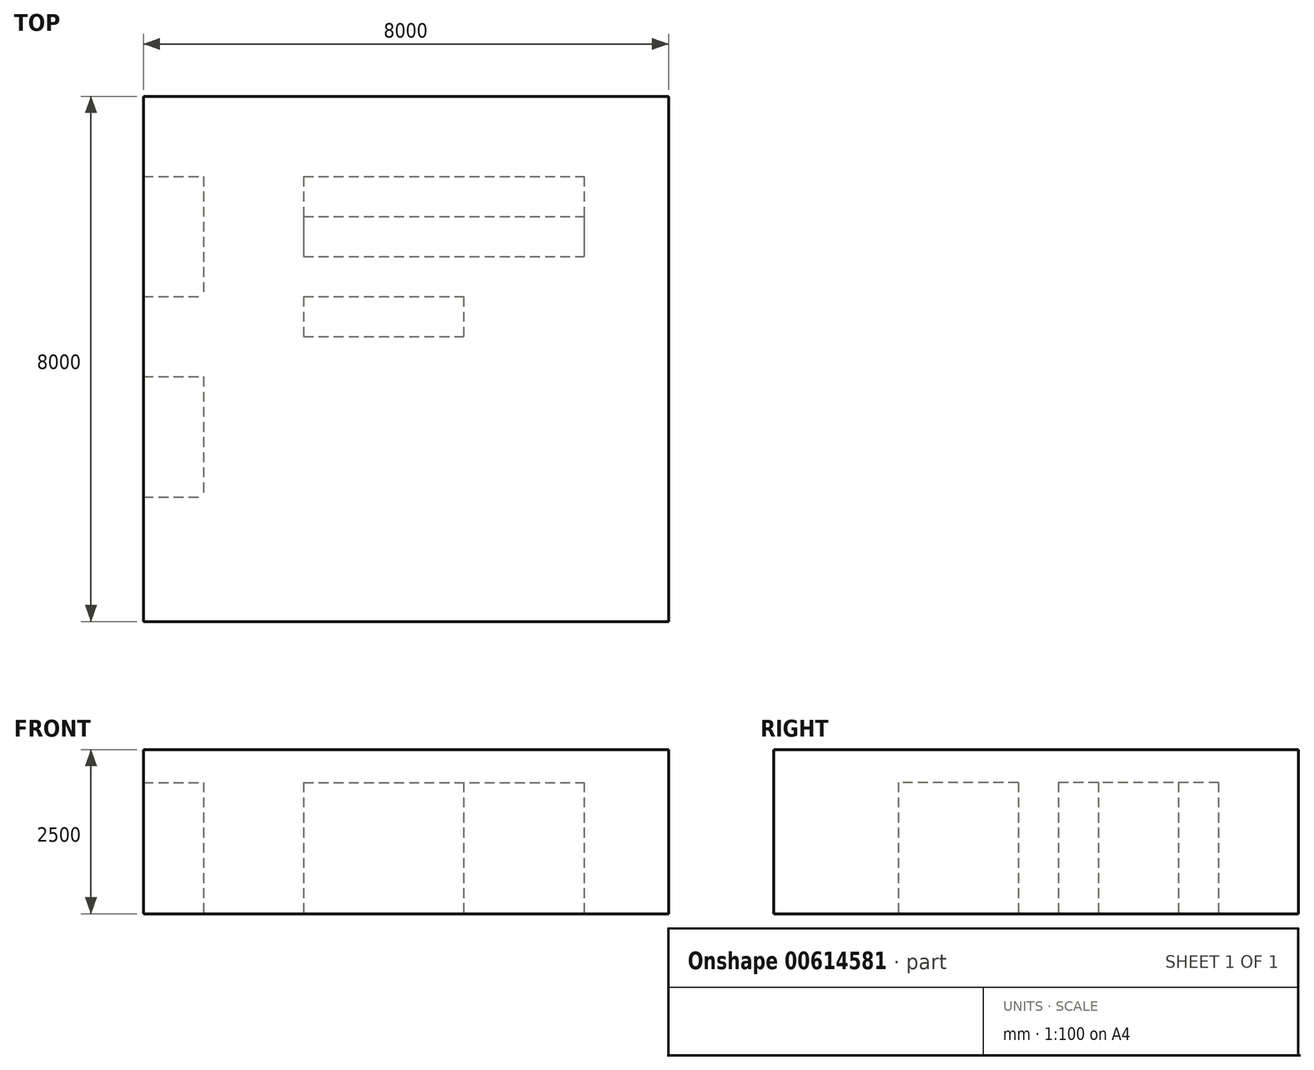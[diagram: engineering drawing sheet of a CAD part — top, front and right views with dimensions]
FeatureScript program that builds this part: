
annotation { "Feature Type Name" : "Feature", "Feature Type Description" : "" }
export const myFeature = defineFeature(function(context is Context, id is Id, definition is map)
    precondition{}
    {
        {
            var Q0;
            Q0=qCreatedBy(makeId("Top.planeOp"),FACE);
            var sketch = newSketch(context, id + "F0", { "sketchPlane" : qUnion([Q0])});
            skLineSegment(sketch, "E0.bottom", {"start": v(0, 0) * mm, "end": v(8000, 0) * mm});
            skLineSegment(sketch, "E0.top", {"start": v(0, -8000) * mm, "end": v(8000, -8000) * mm});
            skLineSegment(sketch, "E0.left", {"start": v(0, 0) * mm, "end": v(0, -8000) * mm});
            skLineSegment(sketch, "E0.right", {"start": v(8000, 0) * mm, "end": v(8000, -8000) * mm});
            skLineSegment(sketch, "E1.bottom", {"start": v(0, 0) * mm, "end": v(610, 0) * mm, "construction": true});
            skLineSegment(sketch, "E1.top", {"start": v(0, -610) * mm, "end": v(610, -610) * mm, "construction": true});
            skLineSegment(sketch, "E1.left", {"start": v(0, 0) * mm, "end": v(0, -610) * mm, "construction": true});
            skLineSegment(sketch, "E1.right", {"start": v(610, 0) * mm, "end": v(610, -610) * mm, "construction": true});
            skLineSegment(sketch, "E2.0.1.0", {"start": v(0, -1220) * mm, "end": v(610, -1220) * mm, "construction": true});
            skLineSegment(sketch, "E2.0.1.1", {"start": v(610, -610) * mm, "end": v(610, -1220) * mm, "construction": true});
            skLineSegment(sketch, "E2.0.2.0", {"start": v(0, -1830) * mm, "end": v(610, -1830) * mm, "construction": true});
            skLineSegment(sketch, "E2.0.2.1", {"start": v(610, -1220) * mm, "end": v(610, -1830) * mm, "construction": true});
            skLineSegment(sketch, "E2.0.3.0", {"start": v(0, -2440) * mm, "end": v(610, -2440) * mm, "construction": true});
            skLineSegment(sketch, "E2.0.3.1", {"start": v(610, -1830) * mm, "end": v(610, -2440) * mm, "construction": true});
            skLineSegment(sketch, "E2.0.4.0", {"start": v(0, -3050) * mm, "end": v(610, -3050) * mm, "construction": true});
            skLineSegment(sketch, "E2.0.4.1", {"start": v(610, -2440) * mm, "end": v(610, -3050) * mm, "construction": true});
            skLineSegment(sketch, "E2.0.5.0", {"start": v(0, -3660) * mm, "end": v(610, -3660) * mm, "construction": true});
            skLineSegment(sketch, "E2.0.5.1", {"start": v(610, -3050) * mm, "end": v(610, -3660) * mm, "construction": true});
            skLineSegment(sketch, "E2.0.6.0", {"start": v(0, -4270) * mm, "end": v(610, -4270) * mm, "construction": true});
            skLineSegment(sketch, "E2.0.6.1", {"start": v(610, -3660) * mm, "end": v(610, -4270) * mm, "construction": true});
            skLineSegment(sketch, "E2.0.7.0", {"start": v(0, -4880) * mm, "end": v(610, -4880) * mm, "construction": true});
            skLineSegment(sketch, "E2.0.7.1", {"start": v(610, -4270) * mm, "end": v(610, -4880) * mm, "construction": true});
            skLineSegment(sketch, "E2.0.8.0", {"start": v(0, -5490) * mm, "end": v(610, -5490) * mm, "construction": true});
            skLineSegment(sketch, "E2.0.8.1", {"start": v(610, -4880) * mm, "end": v(610, -5490) * mm, "construction": true});
            skLineSegment(sketch, "E2.0.9.0", {"start": v(0, -6100) * mm, "end": v(610, -6100) * mm, "construction": true});
            skLineSegment(sketch, "E2.0.9.1", {"start": v(610, -5490) * mm, "end": v(610, -6100) * mm, "construction": true});
            skLineSegment(sketch, "E2.0.10.0", {"start": v(0, -6710) * mm, "end": v(610, -6710) * mm, "construction": true});
            skLineSegment(sketch, "E2.0.10.1", {"start": v(610, -6100) * mm, "end": v(610, -6710) * mm, "construction": true});
            skLineSegment(sketch, "E2.0.11.0", {"start": v(0, -7320) * mm, "end": v(610, -7320) * mm, "construction": true});
            skLineSegment(sketch, "E2.0.11.1", {"start": v(610, -6710) * mm, "end": v(610, -7320) * mm, "construction": true});
            skLineSegment(sketch, "E2.0.12.0", {"start": v(0, -7930) * mm, "end": v(610, -7930) * mm, "construction": true});
            skLineSegment(sketch, "E2.0.12.1", {"start": v(610, -7320) * mm, "end": v(610, -7930) * mm, "construction": true});
            skLineSegment(sketch, "E2.1.0.0", {"start": v(610, -610) * mm, "end": v(1220, -610) * mm, "construction": true});
            skLineSegment(sketch, "E2.1.0.1", {"start": v(1220, 0) * mm, "end": v(1220, -610) * mm, "construction": true});
            skLineSegment(sketch, "E2.1.1.0", {"start": v(610, -1220) * mm, "end": v(1220, -1220) * mm, "construction": true});
            skLineSegment(sketch, "E2.1.1.1", {"start": v(1220, -610) * mm, "end": v(1220, -1220) * mm, "construction": true});
            skLineSegment(sketch, "E2.1.2.0", {"start": v(610, -1830) * mm, "end": v(1220, -1830) * mm, "construction": true});
            skLineSegment(sketch, "E2.1.2.1", {"start": v(1220, -1220) * mm, "end": v(1220, -1830) * mm, "construction": true});
            skLineSegment(sketch, "E2.1.3.0", {"start": v(610, -2440) * mm, "end": v(1220, -2440) * mm, "construction": true});
            skLineSegment(sketch, "E2.1.3.1", {"start": v(1220, -1830) * mm, "end": v(1220, -2440) * mm, "construction": true});
            skLineSegment(sketch, "E2.1.4.0", {"start": v(610, -3050) * mm, "end": v(1220, -3050) * mm, "construction": true});
            skLineSegment(sketch, "E2.1.4.1", {"start": v(1220, -2440) * mm, "end": v(1220, -3050) * mm, "construction": true});
            skLineSegment(sketch, "E2.1.5.0", {"start": v(610, -3660) * mm, "end": v(1220, -3660) * mm, "construction": true});
            skLineSegment(sketch, "E2.1.5.1", {"start": v(1220, -3050) * mm, "end": v(1220, -3660) * mm, "construction": true});
            skLineSegment(sketch, "E2.1.6.0", {"start": v(610, -4270) * mm, "end": v(1220, -4270) * mm, "construction": true});
            skLineSegment(sketch, "E2.1.6.1", {"start": v(1220, -3660) * mm, "end": v(1220, -4270) * mm, "construction": true});
            skLineSegment(sketch, "E2.1.7.0", {"start": v(610, -4880) * mm, "end": v(1220, -4880) * mm, "construction": true});
            skLineSegment(sketch, "E2.1.7.1", {"start": v(1220, -4270) * mm, "end": v(1220, -4880) * mm, "construction": true});
            skLineSegment(sketch, "E2.1.8.0", {"start": v(610, -5490) * mm, "end": v(1220, -5490) * mm, "construction": true});
            skLineSegment(sketch, "E2.1.8.1", {"start": v(1220, -4880) * mm, "end": v(1220, -5490) * mm, "construction": true});
            skLineSegment(sketch, "E2.1.9.0", {"start": v(610, -6100) * mm, "end": v(1220, -6100) * mm, "construction": true});
            skLineSegment(sketch, "E2.1.9.1", {"start": v(1220, -5490) * mm, "end": v(1220, -6100) * mm, "construction": true});
            skLineSegment(sketch, "E2.1.10.0", {"start": v(610, -6710) * mm, "end": v(1220, -6710) * mm, "construction": true});
            skLineSegment(sketch, "E2.1.10.1", {"start": v(1220, -6100) * mm, "end": v(1220, -6710) * mm, "construction": true});
            skLineSegment(sketch, "E2.1.11.0", {"start": v(610, -7320) * mm, "end": v(1220, -7320) * mm, "construction": true});
            skLineSegment(sketch, "E2.1.11.1", {"start": v(1220, -6710) * mm, "end": v(1220, -7320) * mm, "construction": true});
            skLineSegment(sketch, "E2.1.12.0", {"start": v(610, -7930) * mm, "end": v(1220, -7930) * mm, "construction": true});
            skLineSegment(sketch, "E2.1.12.1", {"start": v(1220, -7320) * mm, "end": v(1220, -7930) * mm, "construction": true});
            skLineSegment(sketch, "E2.2.0.0", {"start": v(1220, -610) * mm, "end": v(1830, -610) * mm, "construction": true});
            skLineSegment(sketch, "E2.2.0.1", {"start": v(1830, 0) * mm, "end": v(1830, -610) * mm, "construction": true});
            skLineSegment(sketch, "E2.2.1.0", {"start": v(1220, -1220) * mm, "end": v(1830, -1220) * mm, "construction": true});
            skLineSegment(sketch, "E2.2.1.1", {"start": v(1830, -610) * mm, "end": v(1830, -1220) * mm, "construction": true});
            skLineSegment(sketch, "E2.2.2.0", {"start": v(1220, -1830) * mm, "end": v(1830, -1830) * mm, "construction": true});
            skLineSegment(sketch, "E2.2.2.1", {"start": v(1830, -1220) * mm, "end": v(1830, -1830) * mm, "construction": true});
            skLineSegment(sketch, "E2.2.3.0", {"start": v(1220, -2440) * mm, "end": v(1830, -2440) * mm, "construction": true});
            skLineSegment(sketch, "E2.2.3.1", {"start": v(1830, -1830) * mm, "end": v(1830, -2440) * mm, "construction": true});
            skLineSegment(sketch, "E2.2.4.0", {"start": v(1220, -3050) * mm, "end": v(1830, -3050) * mm, "construction": true});
            skLineSegment(sketch, "E2.2.4.1", {"start": v(1830, -2440) * mm, "end": v(1830, -3050) * mm, "construction": true});
            skLineSegment(sketch, "E2.2.5.0", {"start": v(1220, -3660) * mm, "end": v(1830, -3660) * mm, "construction": true});
            skLineSegment(sketch, "E2.2.5.1", {"start": v(1830, -3050) * mm, "end": v(1830, -3660) * mm, "construction": true});
            skLineSegment(sketch, "E2.2.6.0", {"start": v(1220, -4270) * mm, "end": v(1830, -4270) * mm, "construction": true});
            skLineSegment(sketch, "E2.2.6.1", {"start": v(1830, -3660) * mm, "end": v(1830, -4270) * mm, "construction": true});
            skLineSegment(sketch, "E2.2.7.0", {"start": v(1220, -4880) * mm, "end": v(1830, -4880) * mm, "construction": true});
            skLineSegment(sketch, "E2.2.7.1", {"start": v(1830, -4270) * mm, "end": v(1830, -4880) * mm, "construction": true});
            skLineSegment(sketch, "E2.2.8.0", {"start": v(1220, -5490) * mm, "end": v(1830, -5490) * mm, "construction": true});
            skLineSegment(sketch, "E2.2.8.1", {"start": v(1830, -4880) * mm, "end": v(1830, -5490) * mm, "construction": true});
            skLineSegment(sketch, "E2.2.9.0", {"start": v(1220, -6100) * mm, "end": v(1830, -6100) * mm, "construction": true});
            skLineSegment(sketch, "E2.2.9.1", {"start": v(1830, -5490) * mm, "end": v(1830, -6100) * mm, "construction": true});
            skLineSegment(sketch, "E2.2.10.0", {"start": v(1220, -6710) * mm, "end": v(1830, -6710) * mm, "construction": true});
            skLineSegment(sketch, "E2.2.10.1", {"start": v(1830, -6100) * mm, "end": v(1830, -6710) * mm, "construction": true});
            skLineSegment(sketch, "E2.2.11.0", {"start": v(1220, -7320) * mm, "end": v(1830, -7320) * mm, "construction": true});
            skLineSegment(sketch, "E2.2.11.1", {"start": v(1830, -6710) * mm, "end": v(1830, -7320) * mm, "construction": true});
            skLineSegment(sketch, "E2.2.12.0", {"start": v(1220, -7930) * mm, "end": v(1830, -7930) * mm, "construction": true});
            skLineSegment(sketch, "E2.2.12.1", {"start": v(1830, -7320) * mm, "end": v(1830, -7930) * mm, "construction": true});
            skLineSegment(sketch, "E2.3.0.0", {"start": v(1830, -610) * mm, "end": v(2440, -610) * mm, "construction": true});
            skLineSegment(sketch, "E2.3.0.1", {"start": v(2440, 0) * mm, "end": v(2440, -610) * mm, "construction": true});
            skLineSegment(sketch, "E2.3.1.0", {"start": v(1830, -1220) * mm, "end": v(2440, -1220) * mm, "construction": true});
            skLineSegment(sketch, "E2.3.1.1", {"start": v(2440, -610) * mm, "end": v(2440, -1220) * mm, "construction": true});
            skLineSegment(sketch, "E2.3.2.0", {"start": v(1830, -1830) * mm, "end": v(2440, -1830) * mm, "construction": true});
            skLineSegment(sketch, "E2.3.2.1", {"start": v(2440, -1220) * mm, "end": v(2440, -1830) * mm, "construction": true});
            skLineSegment(sketch, "E2.3.3.0", {"start": v(1830, -2440) * mm, "end": v(2440, -2440) * mm, "construction": true});
            skLineSegment(sketch, "E2.3.3.1", {"start": v(2440, -1830) * mm, "end": v(2440, -2440) * mm, "construction": true});
            skLineSegment(sketch, "E2.3.4.0", {"start": v(1830, -3050) * mm, "end": v(2440, -3050) * mm, "construction": true});
            skLineSegment(sketch, "E2.3.4.1", {"start": v(2440, -2440) * mm, "end": v(2440, -3050) * mm, "construction": true});
            skLineSegment(sketch, "E2.3.5.0", {"start": v(1830, -3660) * mm, "end": v(2440, -3660) * mm, "construction": true});
            skLineSegment(sketch, "E2.3.5.1", {"start": v(2440, -3050) * mm, "end": v(2440, -3660) * mm, "construction": true});
            skLineSegment(sketch, "E2.3.6.0", {"start": v(1830, -4270) * mm, "end": v(2440, -4270) * mm, "construction": true});
            skLineSegment(sketch, "E2.3.6.1", {"start": v(2440, -3660) * mm, "end": v(2440, -4270) * mm, "construction": true});
            skLineSegment(sketch, "E2.3.7.0", {"start": v(1830, -4880) * mm, "end": v(2440, -4880) * mm, "construction": true});
            skLineSegment(sketch, "E2.3.7.1", {"start": v(2440, -4270) * mm, "end": v(2440, -4880) * mm, "construction": true});
            skLineSegment(sketch, "E2.3.8.0", {"start": v(1830, -5490) * mm, "end": v(2440, -5490) * mm, "construction": true});
            skLineSegment(sketch, "E2.3.8.1", {"start": v(2440, -4880) * mm, "end": v(2440, -5490) * mm, "construction": true});
            skLineSegment(sketch, "E2.3.9.0", {"start": v(1830, -6100) * mm, "end": v(2440, -6100) * mm, "construction": true});
            skLineSegment(sketch, "E2.3.9.1", {"start": v(2440, -5490) * mm, "end": v(2440, -6100) * mm, "construction": true});
            skLineSegment(sketch, "E2.3.10.0", {"start": v(1830, -6710) * mm, "end": v(2440, -6710) * mm, "construction": true});
            skLineSegment(sketch, "E2.3.10.1", {"start": v(2440, -6100) * mm, "end": v(2440, -6710) * mm, "construction": true});
            skLineSegment(sketch, "E2.3.11.0", {"start": v(1830, -7320) * mm, "end": v(2440, -7320) * mm, "construction": true});
            skLineSegment(sketch, "E2.3.11.1", {"start": v(2440, -6710) * mm, "end": v(2440, -7320) * mm, "construction": true});
            skLineSegment(sketch, "E2.3.12.0", {"start": v(1830, -7930) * mm, "end": v(2440, -7930) * mm, "construction": true});
            skLineSegment(sketch, "E2.3.12.1", {"start": v(2440, -7320) * mm, "end": v(2440, -7930) * mm, "construction": true});
            skLineSegment(sketch, "E2.4.0.0", {"start": v(2440, -610) * mm, "end": v(3050, -610) * mm, "construction": true});
            skLineSegment(sketch, "E2.4.0.1", {"start": v(3050, 0) * mm, "end": v(3050, -610) * mm, "construction": true});
            skLineSegment(sketch, "E2.4.1.0", {"start": v(2440, -1220) * mm, "end": v(3050, -1220) * mm, "construction": true});
            skLineSegment(sketch, "E2.4.1.1", {"start": v(3050, -610) * mm, "end": v(3050, -1220) * mm, "construction": true});
            skLineSegment(sketch, "E2.4.2.0", {"start": v(2440, -1830) * mm, "end": v(3050, -1830) * mm, "construction": true});
            skLineSegment(sketch, "E2.4.2.1", {"start": v(3050, -1220) * mm, "end": v(3050, -1830) * mm, "construction": true});
            skLineSegment(sketch, "E2.4.3.0", {"start": v(2440, -2440) * mm, "end": v(3050, -2440) * mm, "construction": true});
            skLineSegment(sketch, "E2.4.3.1", {"start": v(3050, -1830) * mm, "end": v(3050, -2440) * mm, "construction": true});
            skLineSegment(sketch, "E2.4.4.0", {"start": v(2440, -3050) * mm, "end": v(3050, -3050) * mm, "construction": true});
            skLineSegment(sketch, "E2.4.4.1", {"start": v(3050, -2440) * mm, "end": v(3050, -3050) * mm, "construction": true});
            skLineSegment(sketch, "E2.4.5.0", {"start": v(2440, -3660) * mm, "end": v(3050, -3660) * mm, "construction": true});
            skLineSegment(sketch, "E2.4.5.1", {"start": v(3050, -3050) * mm, "end": v(3050, -3660) * mm, "construction": true});
            skLineSegment(sketch, "E2.4.6.0", {"start": v(2440, -4270) * mm, "end": v(3050, -4270) * mm, "construction": true});
            skLineSegment(sketch, "E2.4.6.1", {"start": v(3050, -3660) * mm, "end": v(3050, -4270) * mm, "construction": true});
            skLineSegment(sketch, "E2.4.7.0", {"start": v(2440, -4880) * mm, "end": v(3050, -4880) * mm, "construction": true});
            skLineSegment(sketch, "E2.4.7.1", {"start": v(3050, -4270) * mm, "end": v(3050, -4880) * mm, "construction": true});
            skLineSegment(sketch, "E2.4.8.0", {"start": v(2440, -5490) * mm, "end": v(3050, -5490) * mm, "construction": true});
            skLineSegment(sketch, "E2.4.8.1", {"start": v(3050, -4880) * mm, "end": v(3050, -5490) * mm, "construction": true});
            skLineSegment(sketch, "E2.4.9.0", {"start": v(2440, -6100) * mm, "end": v(3050, -6100) * mm, "construction": true});
            skLineSegment(sketch, "E2.4.9.1", {"start": v(3050, -5490) * mm, "end": v(3050, -6100) * mm, "construction": true});
            skLineSegment(sketch, "E2.4.10.0", {"start": v(2440, -6710) * mm, "end": v(3050, -6710) * mm, "construction": true});
            skLineSegment(sketch, "E2.4.10.1", {"start": v(3050, -6100) * mm, "end": v(3050, -6710) * mm, "construction": true});
            skLineSegment(sketch, "E2.4.11.0", {"start": v(2440, -7320) * mm, "end": v(3050, -7320) * mm, "construction": true});
            skLineSegment(sketch, "E2.4.11.1", {"start": v(3050, -6710) * mm, "end": v(3050, -7320) * mm, "construction": true});
            skLineSegment(sketch, "E2.4.12.0", {"start": v(2440, -7930) * mm, "end": v(3050, -7930) * mm, "construction": true});
            skLineSegment(sketch, "E2.4.12.1", {"start": v(3050, -7320) * mm, "end": v(3050, -7930) * mm, "construction": true});
            skLineSegment(sketch, "E2.5.0.0", {"start": v(3050, -610) * mm, "end": v(3660, -610) * mm, "construction": true});
            skLineSegment(sketch, "E2.5.0.1", {"start": v(3660, 0) * mm, "end": v(3660, -610) * mm, "construction": true});
            skLineSegment(sketch, "E2.5.1.0", {"start": v(3050, -1220) * mm, "end": v(3660, -1220) * mm, "construction": true});
            skLineSegment(sketch, "E2.5.1.1", {"start": v(3660, -610) * mm, "end": v(3660, -1220) * mm, "construction": true});
            skLineSegment(sketch, "E2.5.2.0", {"start": v(3050, -1830) * mm, "end": v(3660, -1830) * mm, "construction": true});
            skLineSegment(sketch, "E2.5.2.1", {"start": v(3660, -1220) * mm, "end": v(3660, -1830) * mm, "construction": true});
            skLineSegment(sketch, "E2.5.3.0", {"start": v(3050, -2440) * mm, "end": v(3660, -2440) * mm, "construction": true});
            skLineSegment(sketch, "E2.5.3.1", {"start": v(3660, -1830) * mm, "end": v(3660, -2440) * mm, "construction": true});
            skLineSegment(sketch, "E2.5.4.0", {"start": v(3050, -3050) * mm, "end": v(3660, -3050) * mm, "construction": true});
            skLineSegment(sketch, "E2.5.4.1", {"start": v(3660, -2440) * mm, "end": v(3660, -3050) * mm, "construction": true});
            skLineSegment(sketch, "E2.5.5.0", {"start": v(3050, -3660) * mm, "end": v(3660, -3660) * mm, "construction": true});
            skLineSegment(sketch, "E2.5.5.1", {"start": v(3660, -3050) * mm, "end": v(3660, -3660) * mm, "construction": true});
            skLineSegment(sketch, "E2.5.6.0", {"start": v(3050, -4270) * mm, "end": v(3660, -4270) * mm, "construction": true});
            skLineSegment(sketch, "E2.5.6.1", {"start": v(3660, -3660) * mm, "end": v(3660, -4270) * mm, "construction": true});
            skLineSegment(sketch, "E2.5.7.0", {"start": v(3050, -4880) * mm, "end": v(3660, -4880) * mm, "construction": true});
            skLineSegment(sketch, "E2.5.7.1", {"start": v(3660, -4270) * mm, "end": v(3660, -4880) * mm, "construction": true});
            skLineSegment(sketch, "E2.5.8.0", {"start": v(3050, -5490) * mm, "end": v(3660, -5490) * mm, "construction": true});
            skLineSegment(sketch, "E2.5.8.1", {"start": v(3660, -4880) * mm, "end": v(3660, -5490) * mm, "construction": true});
            skLineSegment(sketch, "E2.5.9.0", {"start": v(3050, -6100) * mm, "end": v(3660, -6100) * mm, "construction": true});
            skLineSegment(sketch, "E2.5.9.1", {"start": v(3660, -5490) * mm, "end": v(3660, -6100) * mm, "construction": true});
            skLineSegment(sketch, "E2.5.10.0", {"start": v(3050, -6710) * mm, "end": v(3660, -6710) * mm, "construction": true});
            skLineSegment(sketch, "E2.5.10.1", {"start": v(3660, -6100) * mm, "end": v(3660, -6710) * mm, "construction": true});
            skLineSegment(sketch, "E2.5.11.0", {"start": v(3050, -7320) * mm, "end": v(3660, -7320) * mm, "construction": true});
            skLineSegment(sketch, "E2.5.11.1", {"start": v(3660, -6710) * mm, "end": v(3660, -7320) * mm, "construction": true});
            skLineSegment(sketch, "E2.5.12.0", {"start": v(3050, -7930) * mm, "end": v(3660, -7930) * mm, "construction": true});
            skLineSegment(sketch, "E2.5.12.1", {"start": v(3660, -7320) * mm, "end": v(3660, -7930) * mm, "construction": true});
            skLineSegment(sketch, "E2.6.0.0", {"start": v(3660, -610) * mm, "end": v(4270, -610) * mm, "construction": true});
            skLineSegment(sketch, "E2.6.0.1", {"start": v(4270, 0) * mm, "end": v(4270, -610) * mm, "construction": true});
            skLineSegment(sketch, "E2.6.1.0", {"start": v(3660, -1220) * mm, "end": v(4270, -1220) * mm, "construction": true});
            skLineSegment(sketch, "E2.6.1.1", {"start": v(4270, -610) * mm, "end": v(4270, -1220) * mm, "construction": true});
            skLineSegment(sketch, "E2.6.2.0", {"start": v(3660, -1830) * mm, "end": v(4270, -1830) * mm, "construction": true});
            skLineSegment(sketch, "E2.6.2.1", {"start": v(4270, -1220) * mm, "end": v(4270, -1830) * mm, "construction": true});
            skLineSegment(sketch, "E2.6.3.0", {"start": v(3660, -2440) * mm, "end": v(4270, -2440) * mm, "construction": true});
            skLineSegment(sketch, "E2.6.3.1", {"start": v(4270, -1830) * mm, "end": v(4270, -2440) * mm, "construction": true});
            skLineSegment(sketch, "E2.6.4.0", {"start": v(3660, -3050) * mm, "end": v(4270, -3050) * mm, "construction": true});
            skLineSegment(sketch, "E2.6.4.1", {"start": v(4270, -2440) * mm, "end": v(4270, -3050) * mm, "construction": true});
            skLineSegment(sketch, "E2.6.5.0", {"start": v(3660, -3660) * mm, "end": v(4270, -3660) * mm, "construction": true});
            skLineSegment(sketch, "E2.6.5.1", {"start": v(4270, -3050) * mm, "end": v(4270, -3660) * mm, "construction": true});
            skLineSegment(sketch, "E2.6.6.0", {"start": v(3660, -4270) * mm, "end": v(4270, -4270) * mm, "construction": true});
            skLineSegment(sketch, "E2.6.6.1", {"start": v(4270, -3660) * mm, "end": v(4270, -4270) * mm, "construction": true});
            skLineSegment(sketch, "E2.6.7.0", {"start": v(3660, -4880) * mm, "end": v(4270, -4880) * mm, "construction": true});
            skLineSegment(sketch, "E2.6.7.1", {"start": v(4270, -4270) * mm, "end": v(4270, -4880) * mm, "construction": true});
            skLineSegment(sketch, "E2.6.8.0", {"start": v(3660, -5490) * mm, "end": v(4270, -5490) * mm, "construction": true});
            skLineSegment(sketch, "E2.6.8.1", {"start": v(4270, -4880) * mm, "end": v(4270, -5490) * mm, "construction": true});
            skLineSegment(sketch, "E2.6.9.0", {"start": v(3660, -6100) * mm, "end": v(4270, -6100) * mm, "construction": true});
            skLineSegment(sketch, "E2.6.9.1", {"start": v(4270, -5490) * mm, "end": v(4270, -6100) * mm, "construction": true});
            skLineSegment(sketch, "E2.6.10.0", {"start": v(3660, -6710) * mm, "end": v(4270, -6710) * mm, "construction": true});
            skLineSegment(sketch, "E2.6.10.1", {"start": v(4270, -6100) * mm, "end": v(4270, -6710) * mm, "construction": true});
            skLineSegment(sketch, "E2.6.11.0", {"start": v(3660, -7320) * mm, "end": v(4270, -7320) * mm, "construction": true});
            skLineSegment(sketch, "E2.6.11.1", {"start": v(4270, -6710) * mm, "end": v(4270, -7320) * mm, "construction": true});
            skLineSegment(sketch, "E2.6.12.0", {"start": v(3660, -7930) * mm, "end": v(4270, -7930) * mm, "construction": true});
            skLineSegment(sketch, "E2.6.12.1", {"start": v(4270, -7320) * mm, "end": v(4270, -7930) * mm, "construction": true});
            skLineSegment(sketch, "E2.7.0.0", {"start": v(4270, -610) * mm, "end": v(4880, -610) * mm, "construction": true});
            skLineSegment(sketch, "E2.7.0.1", {"start": v(4880, 0) * mm, "end": v(4880, -610) * mm, "construction": true});
            skLineSegment(sketch, "E2.7.1.0", {"start": v(4270, -1220) * mm, "end": v(4880, -1220) * mm, "construction": true});
            skLineSegment(sketch, "E2.7.1.1", {"start": v(4880, -610) * mm, "end": v(4880, -1220) * mm, "construction": true});
            skLineSegment(sketch, "E2.7.2.0", {"start": v(4270, -1830) * mm, "end": v(4880, -1830) * mm, "construction": true});
            skLineSegment(sketch, "E2.7.2.1", {"start": v(4880, -1220) * mm, "end": v(4880, -1830) * mm, "construction": true});
            skLineSegment(sketch, "E2.7.3.0", {"start": v(4270, -2440) * mm, "end": v(4880, -2440) * mm, "construction": true});
            skLineSegment(sketch, "E2.7.3.1", {"start": v(4880, -1830) * mm, "end": v(4880, -2440) * mm, "construction": true});
            skLineSegment(sketch, "E2.7.4.0", {"start": v(4270, -3050) * mm, "end": v(4880, -3050) * mm, "construction": true});
            skLineSegment(sketch, "E2.7.4.1", {"start": v(4880, -2440) * mm, "end": v(4880, -3050) * mm, "construction": true});
            skLineSegment(sketch, "E2.7.5.0", {"start": v(4270, -3660) * mm, "end": v(4880, -3660) * mm, "construction": true});
            skLineSegment(sketch, "E2.7.5.1", {"start": v(4880, -3050) * mm, "end": v(4880, -3660) * mm, "construction": true});
            skLineSegment(sketch, "E2.7.6.0", {"start": v(4270, -4270) * mm, "end": v(4880, -4270) * mm, "construction": true});
            skLineSegment(sketch, "E2.7.6.1", {"start": v(4880, -3660) * mm, "end": v(4880, -4270) * mm, "construction": true});
            skLineSegment(sketch, "E2.7.7.0", {"start": v(4270, -4880) * mm, "end": v(4880, -4880) * mm, "construction": true});
            skLineSegment(sketch, "E2.7.7.1", {"start": v(4880, -4270) * mm, "end": v(4880, -4880) * mm, "construction": true});
            skLineSegment(sketch, "E2.7.8.0", {"start": v(4270, -5490) * mm, "end": v(4880, -5490) * mm, "construction": true});
            skLineSegment(sketch, "E2.7.8.1", {"start": v(4880, -4880) * mm, "end": v(4880, -5490) * mm, "construction": true});
            skLineSegment(sketch, "E2.7.9.0", {"start": v(4270, -6100) * mm, "end": v(4880, -6100) * mm, "construction": true});
            skLineSegment(sketch, "E2.7.9.1", {"start": v(4880, -5490) * mm, "end": v(4880, -6100) * mm, "construction": true});
            skLineSegment(sketch, "E2.7.10.0", {"start": v(4270, -6710) * mm, "end": v(4880, -6710) * mm, "construction": true});
            skLineSegment(sketch, "E2.7.10.1", {"start": v(4880, -6100) * mm, "end": v(4880, -6710) * mm, "construction": true});
            skLineSegment(sketch, "E2.7.11.0", {"start": v(4270, -7320) * mm, "end": v(4880, -7320) * mm, "construction": true});
            skLineSegment(sketch, "E2.7.11.1", {"start": v(4880, -6710) * mm, "end": v(4880, -7320) * mm, "construction": true});
            skLineSegment(sketch, "E2.7.12.0", {"start": v(4270, -7930) * mm, "end": v(4880, -7930) * mm, "construction": true});
            skLineSegment(sketch, "E2.7.12.1", {"start": v(4880, -7320) * mm, "end": v(4880, -7930) * mm, "construction": true});
            skLineSegment(sketch, "E2.8.0.0", {"start": v(4880, -610) * mm, "end": v(5490, -610) * mm, "construction": true});
            skLineSegment(sketch, "E2.8.0.1", {"start": v(5490, 0) * mm, "end": v(5490, -610) * mm, "construction": true});
            skLineSegment(sketch, "E2.8.1.0", {"start": v(4880, -1220) * mm, "end": v(5490, -1220) * mm, "construction": true});
            skLineSegment(sketch, "E2.8.1.1", {"start": v(5490, -610) * mm, "end": v(5490, -1220) * mm, "construction": true});
            skLineSegment(sketch, "E2.8.2.0", {"start": v(4880, -1830) * mm, "end": v(5490, -1830) * mm, "construction": true});
            skLineSegment(sketch, "E2.8.2.1", {"start": v(5490, -1220) * mm, "end": v(5490, -1830) * mm, "construction": true});
            skLineSegment(sketch, "E2.8.3.0", {"start": v(4880, -2440) * mm, "end": v(5490, -2440) * mm, "construction": true});
            skLineSegment(sketch, "E2.8.3.1", {"start": v(5490, -1830) * mm, "end": v(5490, -2440) * mm, "construction": true});
            skLineSegment(sketch, "E2.8.4.0", {"start": v(4880, -3050) * mm, "end": v(5490, -3050) * mm, "construction": true});
            skLineSegment(sketch, "E2.8.4.1", {"start": v(5490, -2440) * mm, "end": v(5490, -3050) * mm, "construction": true});
            skLineSegment(sketch, "E2.8.5.0", {"start": v(4880, -3660) * mm, "end": v(5490, -3660) * mm, "construction": true});
            skLineSegment(sketch, "E2.8.5.1", {"start": v(5490, -3050) * mm, "end": v(5490, -3660) * mm, "construction": true});
            skLineSegment(sketch, "E2.8.6.0", {"start": v(4880, -4270) * mm, "end": v(5490, -4270) * mm, "construction": true});
            skLineSegment(sketch, "E2.8.6.1", {"start": v(5490, -3660) * mm, "end": v(5490, -4270) * mm, "construction": true});
            skLineSegment(sketch, "E2.8.7.0", {"start": v(4880, -4880) * mm, "end": v(5490, -4880) * mm, "construction": true});
            skLineSegment(sketch, "E2.8.7.1", {"start": v(5490, -4270) * mm, "end": v(5490, -4880) * mm, "construction": true});
            skLineSegment(sketch, "E2.8.8.0", {"start": v(4880, -5490) * mm, "end": v(5490, -5490) * mm, "construction": true});
            skLineSegment(sketch, "E2.8.8.1", {"start": v(5490, -4880) * mm, "end": v(5490, -5490) * mm, "construction": true});
            skLineSegment(sketch, "E2.8.9.0", {"start": v(4880, -6100) * mm, "end": v(5490, -6100) * mm, "construction": true});
            skLineSegment(sketch, "E2.8.9.1", {"start": v(5490, -5490) * mm, "end": v(5490, -6100) * mm, "construction": true});
            skLineSegment(sketch, "E2.8.10.0", {"start": v(4880, -6710) * mm, "end": v(5490, -6710) * mm, "construction": true});
            skLineSegment(sketch, "E2.8.10.1", {"start": v(5490, -6100) * mm, "end": v(5490, -6710) * mm, "construction": true});
            skLineSegment(sketch, "E2.8.11.0", {"start": v(4880, -7320) * mm, "end": v(5490, -7320) * mm, "construction": true});
            skLineSegment(sketch, "E2.8.11.1", {"start": v(5490, -6710) * mm, "end": v(5490, -7320) * mm, "construction": true});
            skLineSegment(sketch, "E2.8.12.0", {"start": v(4880, -7930) * mm, "end": v(5490, -7930) * mm, "construction": true});
            skLineSegment(sketch, "E2.8.12.1", {"start": v(5490, -7320) * mm, "end": v(5490, -7930) * mm, "construction": true});
            skLineSegment(sketch, "E2.9.0.0", {"start": v(5490, -610) * mm, "end": v(6100, -610) * mm, "construction": true});
            skLineSegment(sketch, "E2.9.0.1", {"start": v(6100, 0) * mm, "end": v(6100, -610) * mm, "construction": true});
            skLineSegment(sketch, "E2.9.1.0", {"start": v(5490, -1220) * mm, "end": v(6100, -1220) * mm, "construction": true});
            skLineSegment(sketch, "E2.9.1.1", {"start": v(6100, -610) * mm, "end": v(6100, -1220) * mm, "construction": true});
            skLineSegment(sketch, "E2.9.2.0", {"start": v(5490, -1830) * mm, "end": v(6100, -1830) * mm, "construction": true});
            skLineSegment(sketch, "E2.9.2.1", {"start": v(6100, -1220) * mm, "end": v(6100, -1830) * mm, "construction": true});
            skLineSegment(sketch, "E2.9.3.0", {"start": v(5490, -2440) * mm, "end": v(6100, -2440) * mm, "construction": true});
            skLineSegment(sketch, "E2.9.3.1", {"start": v(6100, -1830) * mm, "end": v(6100, -2440) * mm, "construction": true});
            skLineSegment(sketch, "E2.9.4.0", {"start": v(5490, -3050) * mm, "end": v(6100, -3050) * mm, "construction": true});
            skLineSegment(sketch, "E2.9.4.1", {"start": v(6100, -2440) * mm, "end": v(6100, -3050) * mm, "construction": true});
            skLineSegment(sketch, "E2.9.5.0", {"start": v(5490, -3660) * mm, "end": v(6100, -3660) * mm, "construction": true});
            skLineSegment(sketch, "E2.9.5.1", {"start": v(6100, -3050) * mm, "end": v(6100, -3660) * mm, "construction": true});
            skLineSegment(sketch, "E2.9.6.0", {"start": v(5490, -4270) * mm, "end": v(6100, -4270) * mm, "construction": true});
            skLineSegment(sketch, "E2.9.6.1", {"start": v(6100, -3660) * mm, "end": v(6100, -4270) * mm, "construction": true});
            skLineSegment(sketch, "E2.9.7.0", {"start": v(5490, -4880) * mm, "end": v(6100, -4880) * mm, "construction": true});
            skLineSegment(sketch, "E2.9.7.1", {"start": v(6100, -4270) * mm, "end": v(6100, -4880) * mm, "construction": true});
            skLineSegment(sketch, "E2.9.8.0", {"start": v(5490, -5490) * mm, "end": v(6100, -5490) * mm, "construction": true});
            skLineSegment(sketch, "E2.9.8.1", {"start": v(6100, -4880) * mm, "end": v(6100, -5490) * mm, "construction": true});
            skLineSegment(sketch, "E2.9.9.0", {"start": v(5490, -6100) * mm, "end": v(6100, -6100) * mm, "construction": true});
            skLineSegment(sketch, "E2.9.9.1", {"start": v(6100, -5490) * mm, "end": v(6100, -6100) * mm, "construction": true});
            skLineSegment(sketch, "E2.9.10.0", {"start": v(5490, -6710) * mm, "end": v(6100, -6710) * mm, "construction": true});
            skLineSegment(sketch, "E2.9.10.1", {"start": v(6100, -6100) * mm, "end": v(6100, -6710) * mm, "construction": true});
            skLineSegment(sketch, "E2.9.11.0", {"start": v(5490, -7320) * mm, "end": v(6100, -7320) * mm, "construction": true});
            skLineSegment(sketch, "E2.9.11.1", {"start": v(6100, -6710) * mm, "end": v(6100, -7320) * mm, "construction": true});
            skLineSegment(sketch, "E2.9.12.0", {"start": v(5490, -7930) * mm, "end": v(6100, -7930) * mm, "construction": true});
            skLineSegment(sketch, "E2.9.12.1", {"start": v(6100, -7320) * mm, "end": v(6100, -7930) * mm, "construction": true});
            skLineSegment(sketch, "E2.10.0.0", {"start": v(6100, -610) * mm, "end": v(6710, -610) * mm, "construction": true});
            skLineSegment(sketch, "E2.10.0.1", {"start": v(6710, 0) * mm, "end": v(6710, -610) * mm, "construction": true});
            skLineSegment(sketch, "E2.10.1.0", {"start": v(6100, -1220) * mm, "end": v(6710, -1220) * mm, "construction": true});
            skLineSegment(sketch, "E2.10.1.1", {"start": v(6710, -610) * mm, "end": v(6710, -1220) * mm, "construction": true});
            skLineSegment(sketch, "E2.10.2.0", {"start": v(6100, -1830) * mm, "end": v(6710, -1830) * mm, "construction": true});
            skLineSegment(sketch, "E2.10.2.1", {"start": v(6710, -1220) * mm, "end": v(6710, -1830) * mm, "construction": true});
            skLineSegment(sketch, "E2.10.3.0", {"start": v(6100, -2440) * mm, "end": v(6710, -2440) * mm, "construction": true});
            skLineSegment(sketch, "E2.10.3.1", {"start": v(6710, -1830) * mm, "end": v(6710, -2440) * mm, "construction": true});
            skLineSegment(sketch, "E2.10.4.0", {"start": v(6100, -3050) * mm, "end": v(6710, -3050) * mm, "construction": true});
            skLineSegment(sketch, "E2.10.4.1", {"start": v(6710, -2440) * mm, "end": v(6710, -3050) * mm, "construction": true});
            skLineSegment(sketch, "E2.10.5.0", {"start": v(6100, -3660) * mm, "end": v(6710, -3660) * mm, "construction": true});
            skLineSegment(sketch, "E2.10.5.1", {"start": v(6710, -3050) * mm, "end": v(6710, -3660) * mm, "construction": true});
            skLineSegment(sketch, "E2.10.6.0", {"start": v(6100, -4270) * mm, "end": v(6710, -4270) * mm, "construction": true});
            skLineSegment(sketch, "E2.10.6.1", {"start": v(6710, -3660) * mm, "end": v(6710, -4270) * mm, "construction": true});
            skLineSegment(sketch, "E2.10.7.0", {"start": v(6100, -4880) * mm, "end": v(6710, -4880) * mm, "construction": true});
            skLineSegment(sketch, "E2.10.7.1", {"start": v(6710, -4270) * mm, "end": v(6710, -4880) * mm, "construction": true});
            skLineSegment(sketch, "E2.10.8.0", {"start": v(6100, -5490) * mm, "end": v(6710, -5490) * mm, "construction": true});
            skLineSegment(sketch, "E2.10.8.1", {"start": v(6710, -4880) * mm, "end": v(6710, -5490) * mm, "construction": true});
            skLineSegment(sketch, "E2.10.9.0", {"start": v(6100, -6100) * mm, "end": v(6710, -6100) * mm, "construction": true});
            skLineSegment(sketch, "E2.10.9.1", {"start": v(6710, -5490) * mm, "end": v(6710, -6100) * mm, "construction": true});
            skLineSegment(sketch, "E2.10.10.0", {"start": v(6100, -6710) * mm, "end": v(6710, -6710) * mm, "construction": true});
            skLineSegment(sketch, "E2.10.10.1", {"start": v(6710, -6100) * mm, "end": v(6710, -6710) * mm, "construction": true});
            skLineSegment(sketch, "E2.10.11.0", {"start": v(6100, -7320) * mm, "end": v(6710, -7320) * mm, "construction": true});
            skLineSegment(sketch, "E2.10.11.1", {"start": v(6710, -6710) * mm, "end": v(6710, -7320) * mm, "construction": true});
            skLineSegment(sketch, "E2.10.12.0", {"start": v(6100, -7930) * mm, "end": v(6710, -7930) * mm, "construction": true});
            skLineSegment(sketch, "E2.10.12.1", {"start": v(6710, -7320) * mm, "end": v(6710, -7930) * mm, "construction": true});
            skLineSegment(sketch, "E2.11.0.0", {"start": v(6710, -610) * mm, "end": v(7320, -610) * mm, "construction": true});
            skLineSegment(sketch, "E2.11.0.1", {"start": v(7320, 0) * mm, "end": v(7320, -610) * mm, "construction": true});
            skLineSegment(sketch, "E2.11.1.0", {"start": v(6710, -1220) * mm, "end": v(7320, -1220) * mm, "construction": true});
            skLineSegment(sketch, "E2.11.1.1", {"start": v(7320, -610) * mm, "end": v(7320, -1220) * mm, "construction": true});
            skLineSegment(sketch, "E2.11.2.0", {"start": v(6710, -1830) * mm, "end": v(7320, -1830) * mm, "construction": true});
            skLineSegment(sketch, "E2.11.2.1", {"start": v(7320, -1220) * mm, "end": v(7320, -1830) * mm, "construction": true});
            skLineSegment(sketch, "E2.11.3.0", {"start": v(6710, -2440) * mm, "end": v(7320, -2440) * mm, "construction": true});
            skLineSegment(sketch, "E2.11.3.1", {"start": v(7320, -1830) * mm, "end": v(7320, -2440) * mm, "construction": true});
            skLineSegment(sketch, "E2.11.4.0", {"start": v(6710, -3050) * mm, "end": v(7320, -3050) * mm, "construction": true});
            skLineSegment(sketch, "E2.11.4.1", {"start": v(7320, -2440) * mm, "end": v(7320, -3050) * mm, "construction": true});
            skLineSegment(sketch, "E2.11.5.0", {"start": v(6710, -3660) * mm, "end": v(7320, -3660) * mm, "construction": true});
            skLineSegment(sketch, "E2.11.5.1", {"start": v(7320, -3050) * mm, "end": v(7320, -3660) * mm, "construction": true});
            skLineSegment(sketch, "E2.11.6.0", {"start": v(6710, -4270) * mm, "end": v(7320, -4270) * mm, "construction": true});
            skLineSegment(sketch, "E2.11.6.1", {"start": v(7320, -3660) * mm, "end": v(7320, -4270) * mm, "construction": true});
            skLineSegment(sketch, "E2.11.7.0", {"start": v(6710, -4880) * mm, "end": v(7320, -4880) * mm, "construction": true});
            skLineSegment(sketch, "E2.11.7.1", {"start": v(7320, -4270) * mm, "end": v(7320, -4880) * mm, "construction": true});
            skLineSegment(sketch, "E2.11.8.0", {"start": v(6710, -5490) * mm, "end": v(7320, -5490) * mm, "construction": true});
            skLineSegment(sketch, "E2.11.8.1", {"start": v(7320, -4880) * mm, "end": v(7320, -5490) * mm, "construction": true});
            skLineSegment(sketch, "E2.11.9.0", {"start": v(6710, -6100) * mm, "end": v(7320, -6100) * mm, "construction": true});
            skLineSegment(sketch, "E2.11.9.1", {"start": v(7320, -5490) * mm, "end": v(7320, -6100) * mm, "construction": true});
            skLineSegment(sketch, "E2.11.10.0", {"start": v(6710, -6710) * mm, "end": v(7320, -6710) * mm, "construction": true});
            skLineSegment(sketch, "E2.11.10.1", {"start": v(7320, -6100) * mm, "end": v(7320, -6710) * mm, "construction": true});
            skLineSegment(sketch, "E2.11.11.0", {"start": v(6710, -7320) * mm, "end": v(7320, -7320) * mm, "construction": true});
            skLineSegment(sketch, "E2.11.11.1", {"start": v(7320, -6710) * mm, "end": v(7320, -7320) * mm, "construction": true});
            skLineSegment(sketch, "E2.11.12.0", {"start": v(6710, -7930) * mm, "end": v(7320, -7930) * mm, "construction": true});
            skLineSegment(sketch, "E2.11.12.1", {"start": v(7320, -7320) * mm, "end": v(7320, -7930) * mm, "construction": true});
            skLineSegment(sketch, "E2.12.0.0", {"start": v(7320, -610) * mm, "end": v(7930, -610) * mm, "construction": true});
            skLineSegment(sketch, "E2.12.0.1", {"start": v(7930, 0) * mm, "end": v(7930, -610) * mm, "construction": true});
            skLineSegment(sketch, "E2.12.1.0", {"start": v(7320, -1220) * mm, "end": v(7930, -1220) * mm, "construction": true});
            skLineSegment(sketch, "E2.12.1.1", {"start": v(7930, -610) * mm, "end": v(7930, -1220) * mm, "construction": true});
            skLineSegment(sketch, "E2.12.2.0", {"start": v(7320, -1830) * mm, "end": v(7930, -1830) * mm, "construction": true});
            skLineSegment(sketch, "E2.12.2.1", {"start": v(7930, -1220) * mm, "end": v(7930, -1830) * mm, "construction": true});
            skLineSegment(sketch, "E2.12.3.0", {"start": v(7320, -2440) * mm, "end": v(7930, -2440) * mm, "construction": true});
            skLineSegment(sketch, "E2.12.3.1", {"start": v(7930, -1830) * mm, "end": v(7930, -2440) * mm, "construction": true});
            skLineSegment(sketch, "E2.12.4.0", {"start": v(7320, -3050) * mm, "end": v(7930, -3050) * mm, "construction": true});
            skLineSegment(sketch, "E2.12.4.1", {"start": v(7930, -2440) * mm, "end": v(7930, -3050) * mm, "construction": true});
            skLineSegment(sketch, "E2.12.5.0", {"start": v(7320, -3660) * mm, "end": v(7930, -3660) * mm, "construction": true});
            skLineSegment(sketch, "E2.12.5.1", {"start": v(7930, -3050) * mm, "end": v(7930, -3660) * mm, "construction": true});
            skLineSegment(sketch, "E2.12.6.0", {"start": v(7320, -4270) * mm, "end": v(7930, -4270) * mm, "construction": true});
            skLineSegment(sketch, "E2.12.6.1", {"start": v(7930, -3660) * mm, "end": v(7930, -4270) * mm, "construction": true});
            skLineSegment(sketch, "E2.12.7.0", {"start": v(7320, -4880) * mm, "end": v(7930, -4880) * mm, "construction": true});
            skLineSegment(sketch, "E2.12.7.1", {"start": v(7930, -4270) * mm, "end": v(7930, -4880) * mm, "construction": true});
            skLineSegment(sketch, "E2.12.8.0", {"start": v(7320, -5490) * mm, "end": v(7930, -5490) * mm, "construction": true});
            skLineSegment(sketch, "E2.12.8.1", {"start": v(7930, -4880) * mm, "end": v(7930, -5490) * mm, "construction": true});
            skLineSegment(sketch, "E2.12.9.0", {"start": v(7320, -6100) * mm, "end": v(7930, -6100) * mm, "construction": true});
            skLineSegment(sketch, "E2.12.9.1", {"start": v(7930, -5490) * mm, "end": v(7930, -6100) * mm, "construction": true});
            skLineSegment(sketch, "E2.12.10.0", {"start": v(7320, -6710) * mm, "end": v(7930, -6710) * mm, "construction": true});
            skLineSegment(sketch, "E2.12.10.1", {"start": v(7930, -6100) * mm, "end": v(7930, -6710) * mm, "construction": true});
            skLineSegment(sketch, "E2.12.11.0", {"start": v(7320, -7320) * mm, "end": v(7930, -7320) * mm, "construction": true});
            skLineSegment(sketch, "E2.12.11.1", {"start": v(7930, -6710) * mm, "end": v(7930, -7320) * mm, "construction": true});
            skLineSegment(sketch, "E2.12.12.0", {"start": v(7320, -7930) * mm, "end": v(7930, -7930) * mm, "construction": true});
            skLineSegment(sketch, "E2.12.12.1", {"start": v(7930, -7320) * mm, "end": v(7930, -7930) * mm, "construction": true});
            skLineSegment(sketch, "E2.direction2", {"start": v(0, -610) * mm, "end": v(0, -1220) * mm, "construction": true});
            skLineSegment(sketch, "E3.bottom", {"start": v(0, -1220) * mm, "end": v(915, -1220) * mm});
            skLineSegment(sketch, "E3.top", {"start": v(0, -3050) * mm, "end": v(915, -3050) * mm});
            skLineSegment(sketch, "E3.left", {"start": v(0, -1220) * mm, "end": v(0, -3050) * mm});
            skLineSegment(sketch, "E3.right", {"start": v(915, -1220) * mm, "end": v(915, -3050) * mm});
            skLineSegment(sketch, "E4.bottom", {"start": v(0, -4270) * mm, "end": v(915, -4270) * mm});
            skLineSegment(sketch, "E4.top", {"start": v(0, -6100) * mm, "end": v(915, -6100) * mm});
            skLineSegment(sketch, "E4.left", {"start": v(0, -4270) * mm, "end": v(0, -6100) * mm});
            skLineSegment(sketch, "E4.right", {"start": v(915, -4270) * mm, "end": v(915, -6100) * mm});
            skLineSegment(sketch, "E5.bottom", {"start": v(2440, -1220) * mm, "end": v(6710, -1220) * mm});
            skLineSegment(sketch, "E5.top", {"start": v(2440, -1830) * mm, "end": v(6710, -1830) * mm});
            skLineSegment(sketch, "E5.left", {"start": v(2440, -1220) * mm, "end": v(2440, -1830) * mm});
            skLineSegment(sketch, "E5.right", {"start": v(6710, -1220) * mm, "end": v(6710, -1830) * mm});
            skLineSegment(sketch, "E6.bottom", {"start": v(2440, -3050) * mm, "end": v(4880, -3050) * mm});
            skLineSegment(sketch, "E6.top", {"start": v(2440, -3660) * mm, "end": v(4880, -3660) * mm});
            skLineSegment(sketch, "E6.left", {"start": v(2440, -3050) * mm, "end": v(2440, -3660) * mm});
            skLineSegment(sketch, "E6.right", {"start": v(4880, -3050) * mm, "end": v(4880, -3660) * mm});
            skLineSegment(sketch, "E7.top", {"start": v(2440, -2440) * mm, "end": v(6710, -2440) * mm});
            skLineSegment(sketch, "E7.left", {"start": v(2440, -1830) * mm, "end": v(2440, -2440) * mm});
            skLineSegment(sketch, "E7.right", {"start": v(6710, -1830) * mm, "end": v(6710, -2440) * mm});
            skSolve(sketch);
        }
        {
            var Q0;
            {var subQ4=sQuery(id+"F0.wireOp",EDGE,"E0.bottom");Q0=makeQuery(id+"F0.imprint","IMPRINT",FACE,{"disambiguationData":[TD([[makeQuery(id+"F0.imprint","IMPRINT",EDGE,{"derivedFrom":subQ4}),-1.0]])]});}
            var Q1;
            {var subQ2=sQuery(id+"F0.wireOp",EDGE,"E4.bottom");Q1=makeQuery(id+"F0.imprint","IMPRINT",FACE,{"disambiguationData":[TD([[makeQuery(id+"F0.imprint","IMPRINT",EDGE,{"derivedFrom":subQ2}),-1.0]])]});}
            var Q2;
            {var subQ0=sQuery(id+"F0.wireOp",EDGE,"E3.bottom");Q2=makeQuery(id+"F0.imprint","IMPRINT",FACE,{"disambiguationData":[TD([[makeQuery(id+"F0.imprint","IMPRINT",EDGE,{"derivedFrom":subQ0}),-1.0]])]});}
            var Q3;
            Q3=makeQuery(id+"F0.imprint","IMPRINT",FACE,{"disambiguationData":[TD([[makeQuery(id+"F0.imprint","IMPRINT",EDGE,{"derivedFrom":sQuery(id+"F0.wireOp",EDGE,"E6.bottom")}),-1.0]])]});
            var Q4;
            Q4=makeQuery(id+"F0.imprint","IMPRINT",FACE,{"disambiguationData":[TD([[makeQuery(id+"F0.imprint","IMPRINT",EDGE,{"derivedFrom":sQuery(id+"F0.wireOp",EDGE,"E5.top")}),-1.0]])]});
            var Q5;
            Q5=makeQuery(id+"F0.imprint","IMPRINT",FACE,{"disambiguationData":[TD([[makeQuery(id+"F0.imprint","IMPRINT",EDGE,{"derivedFrom":sQuery(id+"F0.wireOp",EDGE,"E5.bottom")}),-1.0]])]});
            extrude(context, id + "F1", {"entities" : qUnion([Q0, Q1, Q2, Q3, Q4, Q5]), "depth" : 2500 * mm, "offsetDistance" : 25 * mm});
        }
        {
            var Q0;
            {var subQ2=sQuery(id+"F0.wireOp",EDGE,"E4.bottom");Q0=makeQuery(id+"F0.imprint","IMPRINT",FACE,{"disambiguationData":[TD([[makeQuery(id+"F0.imprint","IMPRINT",EDGE,{"derivedFrom":subQ2}),-1.0]])]});}
            var Q1;
            {var subQ0=sQuery(id+"F0.wireOp",EDGE,"E3.bottom");Q1=makeQuery(id+"F0.imprint","IMPRINT",FACE,{"disambiguationData":[TD([[makeQuery(id+"F0.imprint","IMPRINT",EDGE,{"derivedFrom":subQ0}),-1.0]])]});}
            var Q2;
            Q2=makeQuery(id+"F0.imprint","IMPRINT",FACE,{"disambiguationData":[TD([[makeQuery(id+"F0.imprint","IMPRINT",EDGE,{"derivedFrom":sQuery(id+"F0.wireOp",EDGE,"E6.bottom")}),-1.0]])]});
            var Q3;
            Q3=makeQuery(id+"F0.imprint","IMPRINT",FACE,{"disambiguationData":[TD([[makeQuery(id+"F0.imprint","IMPRINT",EDGE,{"derivedFrom":sQuery(id+"F0.wireOp",EDGE,"E5.bottom")}),-1.0]])]});
            extrude(context, id + "F2", {"entities" : qUnion([Q0, Q1, Q2, Q3]), "operationType" : NewBodyOperationType.REMOVE, "depth" : 2000 * mm, "offsetDistance" : 25 * mm});
        }
        {
            var Q0;
            Q0=makeQuery(id+"F0.imprint","IMPRINT",FACE,{"disambiguationData":[TD([[makeQuery(id+"F0.imprint","IMPRINT",EDGE,{"derivedFrom":sQuery(id+"F0.wireOp",EDGE,"E5.top")}),-1.0]])]});
            extrude(context, id + "F3", {"entities" : qUnion([Q0]), "operationType" : NewBodyOperationType.REMOVE, "depth" : 5 * mm, "offsetDistance" : 25 * mm});
        }
    });
